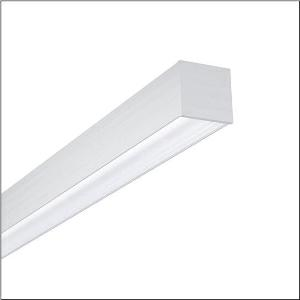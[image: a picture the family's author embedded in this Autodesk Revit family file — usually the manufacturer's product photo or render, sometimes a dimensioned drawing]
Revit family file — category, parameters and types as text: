
# Revit family: silica_r_5mx21bd2e4a_11e7
name_source: partatom
category: Lighting Fixtures
units: mm (PartAtom-declared; Revit-internal decimal feet)

## family parameters
Cut with Voids When Loaded = No
Host = Face
Light Source = No
Part Type = Normal
Room Calculation Point = No
Round Connector Dimension = Use Diameter
Shared = No

## types (1)
- --- (1 x LED, 9910 lm, 60.1 W, 4000K)
    Apparent Load = 60 VA
    CIE Flux Codes = 82 97 100 100 100
    Color Rendering = 80
    Color Temperature = 4000K
    Default Elevation = 1800 mm
    Description = Silica®, office luminaire, of aluminium, light emission: direct distribution, primary light characteristic: symmetric, installation type: surface-mounted, LED, rated luminous flux: 9.910lm, luminous efficacy: 165lm/W, light colour: 840, colour temperature: 4000K, control gear: ECG DALI, with terminal, 3+2-pole, max. 2.5mm², mains connection: 230V, AC, 50/60Hz, rated input power: 60W, luminaire housing, of aluminium, anodised, silver, length: 2.844mm, width: 65mm, height: 64mm, protection rating (complete): IP20, insulation class (complete): insulation class I (protective earthing), certification: CE, permissible operating ambient temperature: 0..+35°C, standard: EN 50419, packaging unit: 1 piece
    Height = 64 mm
    Lamp = 1 x LED
    Lamp Light Flux = 9910 lm
    Lamp Power = 60.1 W
    Lamp count = 1
    Length = 2845 mm
    Luminous efficacy = 165 lm/W
    Manufacturer = Siteco
    ModVariant = No
    Model = 5MX21BD2E4A
    Mounting Place = Ceiling
    Mounting Type = Surface mounted
    Number of Poles = 1
    OnlyDefault = Yes
    Power Factor = 1
    Product Name = Silica®
    Product group = office luminaire | ceiling mounted
    ProductGroupID = 300
    Protection Class = Protection class I
    Protection Degree = IP 20
    RLX_Detail_Level = 1
    RLX_Emergency_Light_Flux = 0 lm
    RLX_Emergency_Type = 0
    RLX_Emergency_Type_DB = No
    RlxData = <blob elided: 27197 chars, md5=19535c34>
    Socket = socket
    Standby Power = 0 W
    System Light Flux = 9910 lm
    System Power = 60 W
    Type Comments = factory setting: luminous flux: 100 % | dim-lin: 254 | 336 mA
    Type Image = l_1004827.jpg
    URL = http://relux.com
    VarID = @adj_155466
    Voltage = 0 V
    Weight = 0.00 kg
    Width = 66 mm

## geometry (parser evidence)
native form markers: Blend x4, Sweep x11
no freeform markers — native parametric forms only
